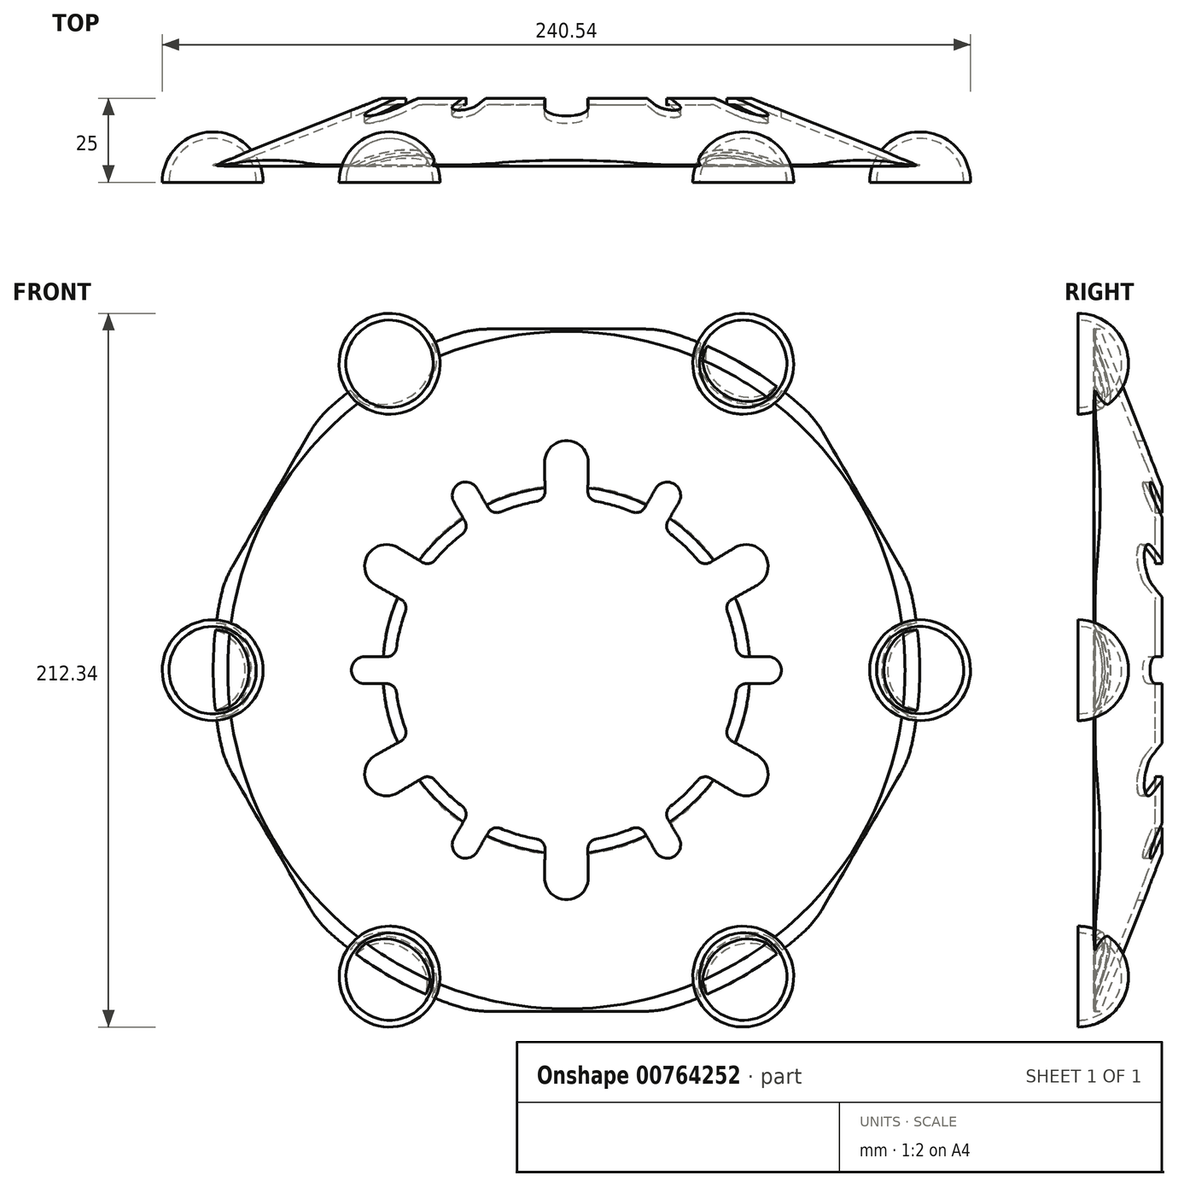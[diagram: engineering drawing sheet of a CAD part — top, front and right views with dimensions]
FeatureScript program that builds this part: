
annotation { "Feature Type Name" : "Feature", "Feature Type Description" : "" }
export const myFeature = defineFeature(function(context is Context, id is Id, definition is map)
    precondition{}
    {
        {
            var Q0;
            Q0=qCreatedBy(makeId("Front.planeOp"),FACE);
            var sketch = newSketch(context, id + "F0", { "sketchPlane" : qUnion([Q0])});
            skCircle(sketch, "E0", {"center": v(0, 0) * mm, "radius": 51 * mm, "construction": true});
            skLineSegment(sketch, "E1", {"start": v(0, 0) * mm, "end": v(0, 51) * mm, "construction": true});
            skLineSegment(sketch, "E2", {"start": v(0, 51) * mm, "end": v(0, 68) * mm, "construction": true});
            skLineSegment(sketch, "E3", {"start": v(0, 68) * mm, "end": v(0, 101.5) * mm, "construction": true});
            skLineSegment(sketch, "E4", {"start": v(0, 0) * mm, "end": v(-25.5, 44.17) * mm, "construction": true});
            skLineSegment(sketch, "E5", {"start": v(-25.5, 44.17) * mm, "end": v(-32, 55.43) * mm, "construction": true});
            skLineSegment(sketch, "E6", {"start": v(-32, 55.43) * mm, "end": v(-52.63, 91.17) * mm, "construction": true});
            skLineSegment(sketch, "E7", {"start": v(-30, 51.96) * mm, "end": v(-26.54, 53.96) * mm, "construction": true});
            skLineSegment(sketch, "E8", {"start": v(0, 61.82) * mm, "end": v(-6.5, 61.72) * mm, "construction": true});
            skLineSegment(sketch, "E9", {"start": v(0, 0) * mm, "end": v(69.25, 119.94) * mm, "construction": true});
            skSolve(sketch);
        }
        {
            var Q0;
            Q0=qCreatedBy(makeId("Right.planeOp"),FACE);
            var Q1;
            Q1=sQuery(id+"F0.wireOp",EDGE,"E4");
            cPlane(context, id + "F1", {"entities" : qUnion([Q0, Q1]), "cplaneType" : CPlaneType.LINE_ANGLE, "offset" : 25 * mm, "angle" : 0 * degree, "width" : 150 * mm, "height" : 150 * mm});
        }
        {
            var Q0;
            Q0=qCreatedBy(makeId("Front.planeOp"),FACE);
            var Q1;
            Q1 = qBodyType(qCreatedBy(id + "F3" ,EDGE), BodyType.WIRE);
            cPlane(context, id + "F2", {"entities" : qUnion([Q0, Q1]), "cplaneType" : CPlaneType.OFFSET, "offset" : 25 * mm, "width" : 150 * mm, "height" : 150 * mm});
        }
        {
            var Q0;
            Q0=qCreatedBy(makeId("Front.planeOp"),FACE);
            var sketch = newSketch(context, id + "F3", { "sketchPlane" : qUnion([Q0])});
            skCircle(sketch, "E10", {"center": v(0, 0) * mm, "radius": 51 * mm, "construction": true});
            skCircle(sketch, "E11", {"center": v(0, 0) * mm, "radius": 101.5 * mm, "construction": true});
            skArc(sketch, "E12", {"start": v(0, 68.32) * mm, "mid": v(-4.63, 66.38) * mm, "end": v(-6.5, 61.72) * mm});
            skArc(sketch, "E13", {"start": v(-26.54, 53.96) * mm, "mid": v(-28.96, 55.83) * mm, "end": v(-32, 55.43) * mm});
            skLineSegment(sketch, "E14", {"start": v(-26.54, 53.96) * mm, "end": v(-23.3, 48.37) * mm});
            skLineSegment(sketch, "E15", {"start": v(-6.5, 61.72) * mm, "end": v(-6.38, 53.22) * mm});
            skArc(sketch, "E16", {"start": v(-8.86, 50.23) * mm, "mid": v(-14.3, 48.96) * mm, "end": v(-19.56, 47.1) * mm});
            skPoint(sketch, "E17.visualSharp", {"position": v(-21.96, 46.03) * mm});
            skArc(sketch, "E17.filletArc", {"start": v(-23.3, 48.37) * mm, "mid": v(-21.67, 47.03) * mm, "end": v(-19.56, 47.1) * mm});
            skArc(sketch, "E18.filletArc", {"start": v(-8.86, 50.23) * mm, "mid": v(-7.06, 51.27) * mm, "end": v(-6.38, 53.22) * mm});
            skLineSegment(sketch, "E19.MirrorCS", {"start": v(6.5, 61.72) * mm, "end": v(6.38, 53.22) * mm});
            skLineSegment(sketch, "E20.MirrorCS", {"start": v(26.54, 53.96) * mm, "end": v(23.3, 48.37) * mm});
            skArc(sketch, "E21.MirrorCS", {"start": v(23.3, 48.37) * mm, "mid": v(21.67, 47.03) * mm, "end": v(19.56, 47.1) * mm});
            skArc(sketch, "E22.MirrorCS", {"start": v(26.54, 53.96) * mm, "mid": v(28.96, 55.83) * mm, "end": v(32, 55.43) * mm});
            skArc(sketch, "E23.MirrorCS", {"start": v(8.86, 50.23) * mm, "mid": v(7.06, 51.27) * mm, "end": v(6.38, 53.22) * mm});
            skArc(sketch, "E24.MirrorCS", {"start": v(8.86, 50.23) * mm, "mid": v(14.3, 48.96) * mm, "end": v(19.56, 47.1) * mm});
            skArc(sketch, "E25.MirrorCS", {"start": v(0, 68.32) * mm, "mid": v(4.63, 66.38) * mm, "end": v(6.5, 61.72) * mm});
            skLineSegment(sketch, "E26", {"start": v(0, 101.5) * mm, "end": v(-23.1, 101.5) * mm});
            skArc(sketch, "E27", {"start": v(-32.33, 100.05) * mm, "mid": v(-42.69, 96.08) * mm, "end": v(-52.57, 91.05) * mm});
            skPoint(sketch, "E28.visualSharp", {"position": v(-27.43, 101.5) * mm});
            skArc(sketch, "E28.filletArc", {"start": v(-23.1, 101.5) * mm, "mid": v(-27.77, 101.13) * mm, "end": v(-32.33, 100.05) * mm});
            skArc(sketch, "E29.MirrorCS", {"start": v(23.1, 101.5) * mm, "mid": v(27.77, 101.13) * mm, "end": v(32.33, 100.05) * mm});
            skLineSegment(sketch, "E30.MirrorCS", {"start": v(0, 101.5) * mm, "end": v(23.1, 101.5) * mm});
            skArc(sketch, "E31.MirrorCS", {"start": v(32.33, 100.05) * mm, "mid": v(42.69, 96.08) * mm, "end": v(52.57, 91.05) * mm});
            skPoint(sketch, "E32.MirrorP", {"position": v(27.43, 101.5) * mm});
            skPoint(sketch, "E33.1.0", {"position": v(-101.61, 27) * mm});
            skLineSegment(sketch, "E33.1.1", {"start": v(-50.2, 36.5) * mm, "end": v(-42.9, 32.13) * mm});
            skPoint(sketch, "E33.1.2", {"position": v(-50.84, 4) * mm});
            skLineSegment(sketch, "E33.1.3", {"start": v(-87.9, 50.75) * mm, "end": v(-99.45, 30.74) * mm});
            skArc(sketch, "E33.1.4", {"start": v(-39.07, 32.78) * mm, "mid": v(-35.25, 36.86) * mm, "end": v(-31.01, 40.49) * mm});
            skArc(sketch, "E33.1.5", {"start": v(-70.48, 78.02) * mm, "mid": v(-61.87, 85) * mm, "end": v(-52.57, 91.05) * mm});
            skPoint(sketch, "E33.1.6", {"position": v(-74.19, 74.5) * mm});
            skLineSegment(sketch, "E33.1.7", {"start": v(-33.46, 49.96) * mm, "end": v(-30.24, 44.37) * mm});
            skLineSegment(sketch, "E33.1.8", {"start": v(-56.7, 25.23) * mm, "end": v(-49.28, 21.09) * mm});
            skLineSegment(sketch, "E33.1.9", {"start": v(-87.9, 50.75) * mm, "end": v(-76.35, 70.76) * mm});
            skLineSegment(sketch, "E33.1.10", {"start": v(-60, 4) * mm, "end": v(-53.54, 4) * mm});
            skArc(sketch, "E33.1.11", {"start": v(-102.8, 22.03) * mm, "mid": v(-104.55, 11.08) * mm, "end": v(-105.14, 0) * mm});
            skArc(sketch, "E33.1.12", {"start": v(-59.16, 34.16) * mm, "mid": v(-59.8, 29.18) * mm, "end": v(-56.7, 25.23) * mm});
            skArc(sketch, "E33.1.13", {"start": v(-59.16, 34.16) * mm, "mid": v(-55.17, 37.2) * mm, "end": v(-50.2, 36.5) * mm});
            skArc(sketch, "E33.1.14", {"start": v(-47.92, 17.44) * mm, "mid": v(-49.54, 12.1) * mm, "end": v(-50.57, 6.61) * mm});
            skArc(sketch, "E33.1.15", {"start": v(-60, 4) * mm, "mid": v(-62.83, 2.83) * mm, "end": v(-64, 0) * mm});
            skArc(sketch, "E33.1.16", {"start": v(-99.45, 30.74) * mm, "mid": v(-101.47, 26.52) * mm, "end": v(-102.8, 22.03) * mm});
            skArc(sketch, "E33.1.17", {"start": v(-76.35, 70.76) * mm, "mid": v(-73.7, 74.62) * mm, "end": v(-70.48, 78.02) * mm});
            skArc(sketch, "E33.1.18", {"start": v(-33.46, 49.96) * mm, "mid": v(-33.86, 53) * mm, "end": v(-32, 55.43) * mm});
            skArc(sketch, "E33.1.19", {"start": v(-47.92, 17.44) * mm, "mid": v(-47.93, 19.52) * mm, "end": v(-49.28, 21.09) * mm});
            skArc(sketch, "E33.1.20", {"start": v(-30.24, 44.37) * mm, "mid": v(-29.9, 42.28) * mm, "end": v(-31.01, 40.49) * mm});
            skArc(sketch, "E33.1.21", {"start": v(-53.54, 4) * mm, "mid": v(-51.57, 4.75) * mm, "end": v(-50.57, 6.61) * mm});
            skArc(sketch, "E33.1.22", {"start": v(-39.07, 32.78) * mm, "mid": v(-40.87, 31.75) * mm, "end": v(-42.9, 32.13) * mm});
            skPoint(sketch, "E33.2.0", {"position": v(-74.19, -74.5) * mm});
            skLineSegment(sketch, "E33.2.1", {"start": v(-56.7, -25.23) * mm, "end": v(-49.28, -21.09) * mm});
            skPoint(sketch, "E33.2.2", {"position": v(-28.89, -42.03) * mm});
            skLineSegment(sketch, "E33.2.3", {"start": v(-87.9, -50.75) * mm, "end": v(-76.35, -70.76) * mm});
            skArc(sketch, "E33.2.4", {"start": v(-47.92, -17.44) * mm, "mid": v(-49.54, -12.1) * mm, "end": v(-50.57, -6.61) * mm});
            skArc(sketch, "E33.2.5", {"start": v(-102.8, -22.03) * mm, "mid": v(-104.55, -11.08) * mm, "end": v(-105.14, 0) * mm});
            skPoint(sketch, "E33.2.6", {"position": v(-101.61, -27) * mm});
            skLineSegment(sketch, "E33.2.7", {"start": v(-60, -4) * mm, "end": v(-53.54, -4) * mm});
            skLineSegment(sketch, "E33.2.8", {"start": v(-50.2, -36.5) * mm, "end": v(-42.9, -32.13) * mm});
            skLineSegment(sketch, "E33.2.9", {"start": v(-87.9, -50.75) * mm, "end": v(-99.45, -30.74) * mm});
            skLineSegment(sketch, "E33.2.10", {"start": v(-33.46, -49.96) * mm, "end": v(-30.24, -44.37) * mm});
            skArc(sketch, "E33.2.11", {"start": v(-70.48, -78.02) * mm, "mid": v(-61.87, -85) * mm, "end": v(-52.57, -91.05) * mm});
            skArc(sketch, "E33.2.12", {"start": v(-59.16, -34.16) * mm, "mid": v(-55.17, -37.2) * mm, "end": v(-50.2, -36.5) * mm});
            skArc(sketch, "E33.2.13", {"start": v(-59.16, -34.16) * mm, "mid": v(-59.8, -29.18) * mm, "end": v(-56.7, -25.23) * mm});
            skArc(sketch, "E33.2.14", {"start": v(-39.07, -32.78) * mm, "mid": v(-35.25, -36.86) * mm, "end": v(-31.01, -40.49) * mm});
            skArc(sketch, "E33.2.15", {"start": v(-33.46, -49.96) * mm, "mid": v(-33.86, -53) * mm, "end": v(-32, -55.43) * mm});
            skArc(sketch, "E33.2.16", {"start": v(-76.35, -70.76) * mm, "mid": v(-73.7, -74.62) * mm, "end": v(-70.48, -78.02) * mm});
            skArc(sketch, "E33.2.17", {"start": v(-99.45, -30.74) * mm, "mid": v(-101.47, -26.52) * mm, "end": v(-102.8, -22.03) * mm});
            skArc(sketch, "E33.2.18", {"start": v(-60, -4) * mm, "mid": v(-62.83, -2.83) * mm, "end": v(-64, 0) * mm});
            skArc(sketch, "E33.2.19", {"start": v(-39.07, -32.78) * mm, "mid": v(-40.87, -31.75) * mm, "end": v(-42.9, -32.13) * mm});
            skArc(sketch, "E33.2.20", {"start": v(-53.54, -4) * mm, "mid": v(-51.57, -4.75) * mm, "end": v(-50.57, -6.61) * mm});
            skArc(sketch, "E33.2.21", {"start": v(-30.24, -44.37) * mm, "mid": v(-29.9, -42.28) * mm, "end": v(-31.01, -40.49) * mm});
            skArc(sketch, "E33.2.22", {"start": v(-47.92, -17.44) * mm, "mid": v(-47.93, -19.52) * mm, "end": v(-49.28, -21.09) * mm});
            skPoint(sketch, "E33.3.0", {"position": v(27.43, -101.5) * mm});
            skLineSegment(sketch, "E33.3.1", {"start": v(-6.5, -61.72) * mm, "end": v(-6.38, -53.22) * mm});
            skPoint(sketch, "E33.3.2", {"position": v(21.96, -46.03) * mm});
            skLineSegment(sketch, "E33.3.3", {"start": v(0, -101.5) * mm, "end": v(23.1, -101.5) * mm});
            skArc(sketch, "E33.3.4", {"start": v(-8.86, -50.23) * mm, "mid": v(-14.3, -48.96) * mm, "end": v(-19.56, -47.1) * mm});
            skArc(sketch, "E33.3.5", {"start": v(-32.33, -100.05) * mm, "mid": v(-42.69, -96.08) * mm, "end": v(-52.57, -91.05) * mm});
            skPoint(sketch, "E33.3.6", {"position": v(-27.43, -101.5) * mm});
            skLineSegment(sketch, "E33.3.7", {"start": v(-26.54, -53.96) * mm, "end": v(-23.3, -48.37) * mm});
            skLineSegment(sketch, "E33.3.8", {"start": v(6.5, -61.72) * mm, "end": v(6.38, -53.22) * mm});
            skLineSegment(sketch, "E33.3.9", {"start": v(0, -101.5) * mm, "end": v(-23.1, -101.5) * mm});
            skLineSegment(sketch, "E33.3.10", {"start": v(26.54, -53.96) * mm, "end": v(23.3, -48.37) * mm});
            skArc(sketch, "E33.3.11", {"start": v(32.33, -100.05) * mm, "mid": v(42.69, -96.08) * mm, "end": v(52.57, -91.05) * mm});
            skArc(sketch, "E33.3.12", {"start": v(0, -68.32) * mm, "mid": v(4.63, -66.38) * mm, "end": v(6.5, -61.72) * mm});
            skArc(sketch, "E33.3.13", {"start": v(0, -68.32) * mm, "mid": v(-4.63, -66.38) * mm, "end": v(-6.5, -61.72) * mm});
            skArc(sketch, "E33.3.14", {"start": v(8.86, -50.23) * mm, "mid": v(14.3, -48.96) * mm, "end": v(19.56, -47.1) * mm});
            skArc(sketch, "E33.3.15", {"start": v(26.54, -53.96) * mm, "mid": v(28.96, -55.83) * mm, "end": v(32, -55.43) * mm});
            skArc(sketch, "E33.3.16", {"start": v(23.1, -101.5) * mm, "mid": v(27.77, -101.13) * mm, "end": v(32.33, -100.05) * mm});
            skArc(sketch, "E33.3.17", {"start": v(-23.1, -101.5) * mm, "mid": v(-27.77, -101.13) * mm, "end": v(-32.33, -100.05) * mm});
            skArc(sketch, "E33.3.18", {"start": v(-26.54, -53.96) * mm, "mid": v(-28.96, -55.83) * mm, "end": v(-32, -55.43) * mm});
            skArc(sketch, "E33.3.19", {"start": v(8.86, -50.23) * mm, "mid": v(7.06, -51.27) * mm, "end": v(6.38, -53.22) * mm});
            skArc(sketch, "E33.3.20", {"start": v(-23.3, -48.37) * mm, "mid": v(-21.67, -47.03) * mm, "end": v(-19.56, -47.1) * mm});
            skArc(sketch, "E33.3.21", {"start": v(23.3, -48.37) * mm, "mid": v(21.67, -47.03) * mm, "end": v(19.56, -47.1) * mm});
            skArc(sketch, "E33.3.22", {"start": v(-8.86, -50.23) * mm, "mid": v(-7.06, -51.27) * mm, "end": v(-6.38, -53.22) * mm});
            skPoint(sketch, "E33.4.0", {"position": v(101.61, -27) * mm});
            skLineSegment(sketch, "E33.4.1", {"start": v(50.2, -36.5) * mm, "end": v(42.9, -32.13) * mm});
            skPoint(sketch, "E33.4.2", {"position": v(50.84, -4) * mm});
            skLineSegment(sketch, "E33.4.3", {"start": v(87.9, -50.75) * mm, "end": v(99.45, -30.74) * mm});
            skArc(sketch, "E33.4.4", {"start": v(39.07, -32.78) * mm, "mid": v(35.25, -36.86) * mm, "end": v(31.01, -40.49) * mm});
            skArc(sketch, "E33.4.5", {"start": v(70.48, -78.02) * mm, "mid": v(61.87, -85) * mm, "end": v(52.57, -91.05) * mm});
            skPoint(sketch, "E33.4.6", {"position": v(74.19, -74.5) * mm});
            skLineSegment(sketch, "E33.4.7", {"start": v(33.46, -49.96) * mm, "end": v(30.24, -44.37) * mm});
            skLineSegment(sketch, "E33.4.8", {"start": v(56.7, -25.23) * mm, "end": v(49.28, -21.09) * mm});
            skLineSegment(sketch, "E33.4.9", {"start": v(87.9, -50.75) * mm, "end": v(76.35, -70.76) * mm});
            skLineSegment(sketch, "E33.4.10", {"start": v(60, -4) * mm, "end": v(53.54, -4) * mm});
            skArc(sketch, "E33.4.11", {"start": v(102.8, -22.03) * mm, "mid": v(104.55, -11.08) * mm, "end": v(105.14, 0) * mm});
            skArc(sketch, "E33.4.12", {"start": v(59.16, -34.16) * mm, "mid": v(59.8, -29.18) * mm, "end": v(56.7, -25.23) * mm});
            skArc(sketch, "E33.4.13", {"start": v(59.16, -34.16) * mm, "mid": v(55.17, -37.2) * mm, "end": v(50.2, -36.5) * mm});
            skArc(sketch, "E33.4.14", {"start": v(47.92, -17.44) * mm, "mid": v(49.54, -12.1) * mm, "end": v(50.57, -6.61) * mm});
            skArc(sketch, "E33.4.15", {"start": v(60, -4) * mm, "mid": v(62.83, -2.83) * mm, "end": v(64, 0) * mm});
            skArc(sketch, "E33.4.16", {"start": v(99.45, -30.74) * mm, "mid": v(101.47, -26.52) * mm, "end": v(102.8, -22.03) * mm});
            skArc(sketch, "E33.4.17", {"start": v(76.35, -70.76) * mm, "mid": v(73.7, -74.62) * mm, "end": v(70.48, -78.02) * mm});
            skArc(sketch, "E33.4.18", {"start": v(33.46, -49.96) * mm, "mid": v(33.86, -53) * mm, "end": v(32, -55.43) * mm});
            skArc(sketch, "E33.4.19", {"start": v(47.92, -17.44) * mm, "mid": v(47.93, -19.52) * mm, "end": v(49.28, -21.09) * mm});
            skArc(sketch, "E33.4.20", {"start": v(30.24, -44.37) * mm, "mid": v(29.9, -42.28) * mm, "end": v(31.01, -40.49) * mm});
            skArc(sketch, "E33.4.21", {"start": v(53.54, -4) * mm, "mid": v(51.57, -4.75) * mm, "end": v(50.57, -6.61) * mm});
            skArc(sketch, "E33.4.22", {"start": v(39.07, -32.78) * mm, "mid": v(40.87, -31.75) * mm, "end": v(42.9, -32.13) * mm});
            skPoint(sketch, "E33.5.0", {"position": v(74.19, 74.5) * mm});
            skLineSegment(sketch, "E33.5.1", {"start": v(56.7, 25.23) * mm, "end": v(49.28, 21.09) * mm});
            skPoint(sketch, "E33.5.2", {"position": v(28.89, 42.03) * mm});
            skLineSegment(sketch, "E33.5.3", {"start": v(87.9, 50.75) * mm, "end": v(76.35, 70.76) * mm});
            skArc(sketch, "E33.5.4", {"start": v(47.92, 17.44) * mm, "mid": v(49.54, 12.1) * mm, "end": v(50.57, 6.61) * mm});
            skArc(sketch, "E33.5.5", {"start": v(102.8, 22.03) * mm, "mid": v(104.55, 11.08) * mm, "end": v(105.14, 0) * mm});
            skPoint(sketch, "E33.5.6", {"position": v(101.61, 27) * mm});
            skLineSegment(sketch, "E33.5.7", {"start": v(60, 4) * mm, "end": v(53.54, 4) * mm});
            skLineSegment(sketch, "E33.5.8", {"start": v(50.2, 36.5) * mm, "end": v(42.9, 32.13) * mm});
            skLineSegment(sketch, "E33.5.9", {"start": v(87.9, 50.75) * mm, "end": v(99.45, 30.74) * mm});
            skLineSegment(sketch, "E33.5.10", {"start": v(33.46, 49.96) * mm, "end": v(30.24, 44.37) * mm});
            skArc(sketch, "E33.5.11", {"start": v(70.48, 78.02) * mm, "mid": v(61.87, 85) * mm, "end": v(52.57, 91.05) * mm});
            skArc(sketch, "E33.5.12", {"start": v(59.16, 34.16) * mm, "mid": v(55.17, 37.2) * mm, "end": v(50.2, 36.5) * mm});
            skArc(sketch, "E33.5.13", {"start": v(59.16, 34.16) * mm, "mid": v(59.8, 29.18) * mm, "end": v(56.7, 25.23) * mm});
            skArc(sketch, "E33.5.14", {"start": v(39.07, 32.78) * mm, "mid": v(35.25, 36.86) * mm, "end": v(31.01, 40.49) * mm});
            skArc(sketch, "E33.5.15", {"start": v(33.46, 49.96) * mm, "mid": v(33.86, 53) * mm, "end": v(32, 55.43) * mm});
            skArc(sketch, "E33.5.16", {"start": v(76.35, 70.76) * mm, "mid": v(73.7, 74.62) * mm, "end": v(70.48, 78.02) * mm});
            skArc(sketch, "E33.5.17", {"start": v(99.45, 30.74) * mm, "mid": v(101.47, 26.52) * mm, "end": v(102.8, 22.03) * mm});
            skArc(sketch, "E33.5.18", {"start": v(60, 4) * mm, "mid": v(62.83, 2.83) * mm, "end": v(64, 0) * mm});
            skArc(sketch, "E33.5.19", {"start": v(39.07, 32.78) * mm, "mid": v(40.87, 31.75) * mm, "end": v(42.9, 32.13) * mm});
            skArc(sketch, "E33.5.20", {"start": v(53.54, 4) * mm, "mid": v(51.57, 4.75) * mm, "end": v(50.57, 6.61) * mm});
            skArc(sketch, "E33.5.21", {"start": v(30.24, 44.37) * mm, "mid": v(29.9, 42.28) * mm, "end": v(31.01, 40.49) * mm});
            skArc(sketch, "E33.5.22", {"start": v(47.92, 17.44) * mm, "mid": v(47.93, 19.52) * mm, "end": v(49.28, 21.09) * mm});
            skSolve(sketch);
        }
        {
            var Q0;
            Q0=makeQuery(id+"F3.imprint","IMPRINT",FACE,{"disambiguationData":[TD([[makeQuery(id+"F3.imprint","IMPRINT",EDGE,{"derivedFrom":sQuery(id+"F3.wireOp",EDGE,"E12")}),-1.0]])]});
            extrude(context, id + "F4", {"entities" : qUnion([Q0]), "depth" : 40 * mm, "offsetDistance" : 25 * mm});
        }
        {
            var Q0;
            Q0=qCreatedBy(id+"F1.planeOp",FACE);
            var sketch = newSketch(context, id + "F5", { "sketchPlane" : qUnion([Q0])});
            skLineSegment(sketch, "E34", {"start": v(0, 105.5) * mm, "end": v(20, 105.5) * mm, "construction": true});
            skPoint(sketch, "E35", {"position": v(0, 51) * mm});
            skPoint(sketch, "E36", {"position": v(0, 55) * mm});
            skLineSegment(sketch, "E37", {"start": v(0, 51) * mm, "end": v(0, 55) * mm});
            skLineSegment(sketch, "E38", {"start": v(0, 55) * mm, "end": v(0, 105.5) * mm, "construction": true});
            skLineSegment(sketch, "E39", {"start": v(0, 55) * mm, "end": v(20, 105.5) * mm});
            skLineSegment(sketch, "E40", {"start": v(0, 51) * mm, "end": v(2, 51) * mm});
            skLineSegment(sketch, "E41.0", {"start": v(2, 54.62) * mm, "end": v(20.28, 100.77) * mm});
            skLineSegment(sketch, "E41.1", {"start": v(2, 51) * mm, "end": v(2, 54.62) * mm});
            skLineSegment(sketch, "E42", {"start": v(20, 105.5) * mm, "end": v(20.28, 100.77) * mm});
            skLineSegment(sketch, "E43", {"start": v(0, 0) * mm, "end": v(-27.43, 0) * mm, "construction": true});
            skSolve(sketch);
        }
        {
            var Q0;
            Q0=qCreatedBy(id+"F2.planeOp",FACE);
            var sketch = newSketch(context, id + "F6", { "sketchPlane" : qUnion([Q0])});
            skPoint(sketch, "E44", {"position": v(-45.14, 78.17) * mm});
            skPoint(sketch, "E45", {"position": v(-60.14, 104.15) * mm});
            skArc(sketch, "E46", {"start": v(-60.14, 104.15) * mm, "mid": v(-65.63, 83.66) * mm, "end": v(-45.14, 78.17) * mm});
            skLineSegment(sketch, "E47", {"start": v(-45.14, 78.17) * mm, "end": v(-60.14, 104.15) * mm});
            skArc(sketch, "E48", {"start": v(-46.14, 79.9) * mm, "mid": v(-63.9, 84.66) * mm, "end": v(-59.14, 102.42) * mm, "construction": true});
            skSolve(sketch);
        }
        {
            var Q0;
            Q0=makeQuery(id+"F5.imprint","IMPRINT",FACE,{"disambiguationData":[TD([[makeQuery(id+"F5.imprint","IMPRINT",EDGE,{"derivedFrom":sQuery(id+"F5.wireOp",EDGE,"E37")}),-1.0]])]});
            var Q1;
            Q1=sQuery(id+"F5.wireOp",EDGE,"E43");
            revolve(context, id + "F7", {"operationType" : NewBodyOperationType.INTERSECT, "surfaceOperationType" : NewSurfaceOperationType.NEW, "entities" : qUnion([Q0]), "axis" : qUnion([Q1]), "revolveType" : RevolveType.FULL});
        }
        {
            var Q0;
            Q0=makeQuery(id+"F6.imprint","IMPRINT",FACE,{"disambiguationData":[TD([[makeQuery(id+"F6.imprint","IMPRINT",EDGE,{"derivedFrom":sQuery(id+"F6.wireOp",EDGE,"E46")}),1.0]])]});
            var Q1;
            Q1=sQuery(id+"F6.wireOp",EDGE,"E47");
            revolve(context, id + "F8", {"surfaceOperationType" : NewSurfaceOperationType.NEW, "entities" : qUnion([Q0]), "axis" : qUnion([Q1]), "revolveType" : RevolveType.ONE_DIRECTION, "oppositeDirection" : true, "angle" : 180 * degree});
        }
        {
            var Q0;
            Q0=makeQuery(id+"F8.opRevolve","CAP_FACE",FACE,{"disambiguationData":[OSD([sQuery(id+"F6.wireOp",EDGE,"E46"),sQuery(id+"F6.wireOp",EDGE,"E47")])],"isStart":true});
            var sketch = newSketch(context, id + "F9", { "sketchPlane" : qUnion([Q0])});
            skCircle(sketch, "E49", {"center": v(-52.64, 91.16) * mm, "radius": 13 * mm, "construction": true});
            skLineSegment(sketch, "E50", {"start": v(-59.15, 102.42) * mm, "end": v(-46.13, 79.91) * mm});
            skArc(sketch, "E51", {"start": v(-46.13, 79.91) * mm, "mid": v(-63.89, 84.65) * mm, "end": v(-59.15, 102.42) * mm});
            skSolve(sketch);
        }
        {
            var Q0;
            Q0=makeQuery(id+"F9.imprint","IMPRINT",FACE,{"disambiguationData":[TD([[makeQuery(id+"F9.imprint","IMPRINT",EDGE,{"derivedFrom":sQuery(id+"F9.wireOp",EDGE,"E50")}),-1.0]])]});
            var Q1;
            Q1=sQuery(id+"F9.wireOp",EDGE,"E50");
            revolve(context, id + "F10", {"operationType" : NewBodyOperationType.REMOVE, "surfaceOperationType" : NewSurfaceOperationType.NEW, "entities" : qUnion([Q0]), "axis" : qUnion([Q1]), "revolveType" : RevolveType.FULL, "oppositeDirection" : true});
        }
        {
            var Q0;
            Q0=makeQuery(id+"F8.opRevolve","SWEPT_BODY",BODY,{"disambiguationData":[OSD([sQuery(id+"F6.wireOp",EDGE,"E46"),sQuery(id+"F6.wireOp",EDGE,"E47")])]});
            var Q1;
            Q1=makeQuery(id+"F10.opRevolve","SWEPT_BODY",BODY,{"disambiguationData":[OSD([sQuery(id+"F9.wireOp",EDGE,"E50"),sQuery(id+"F9.wireOp",EDGE,"E51")])]});
            var Q2;
            Q2=sQuery(id+"F5.wireOp",EDGE,"E43");
            circularPattern(context, id + "F11", {"operationType" : NewBodyOperationType.ADD, "entities" : qUnion([Q0, Q1]), "axis" : qUnion([Q2]), "angle" : 360 * degree, "instanceCount" : 6, "equalSpace" : true});
        }
    });
